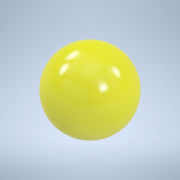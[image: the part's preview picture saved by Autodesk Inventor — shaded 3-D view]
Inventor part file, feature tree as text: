
AUTODESK INVENTOR PART (.ipt)
format: ipt  version: 2020 (Build 240168000, 168)  size: 126,464 bytes
history: native  units: in
note: dims shown in document units (in); Inventor stores cm internally (conversion verified against a paired STEP export)
features: revolve x1, sketch x1
ambient origin geometry x8: Origin, YZ Plane, XZ Plane, XY Plane, X Axis, Y Axis, Z Axis, Center Point
bodies: Solid1 (feature_tree)
feature tree (2):
  revolve  "Revolution1"  Angle=90.0deg
  sketch  "Sketch1"  dims[d0=7.0in d1=90.0deg]
